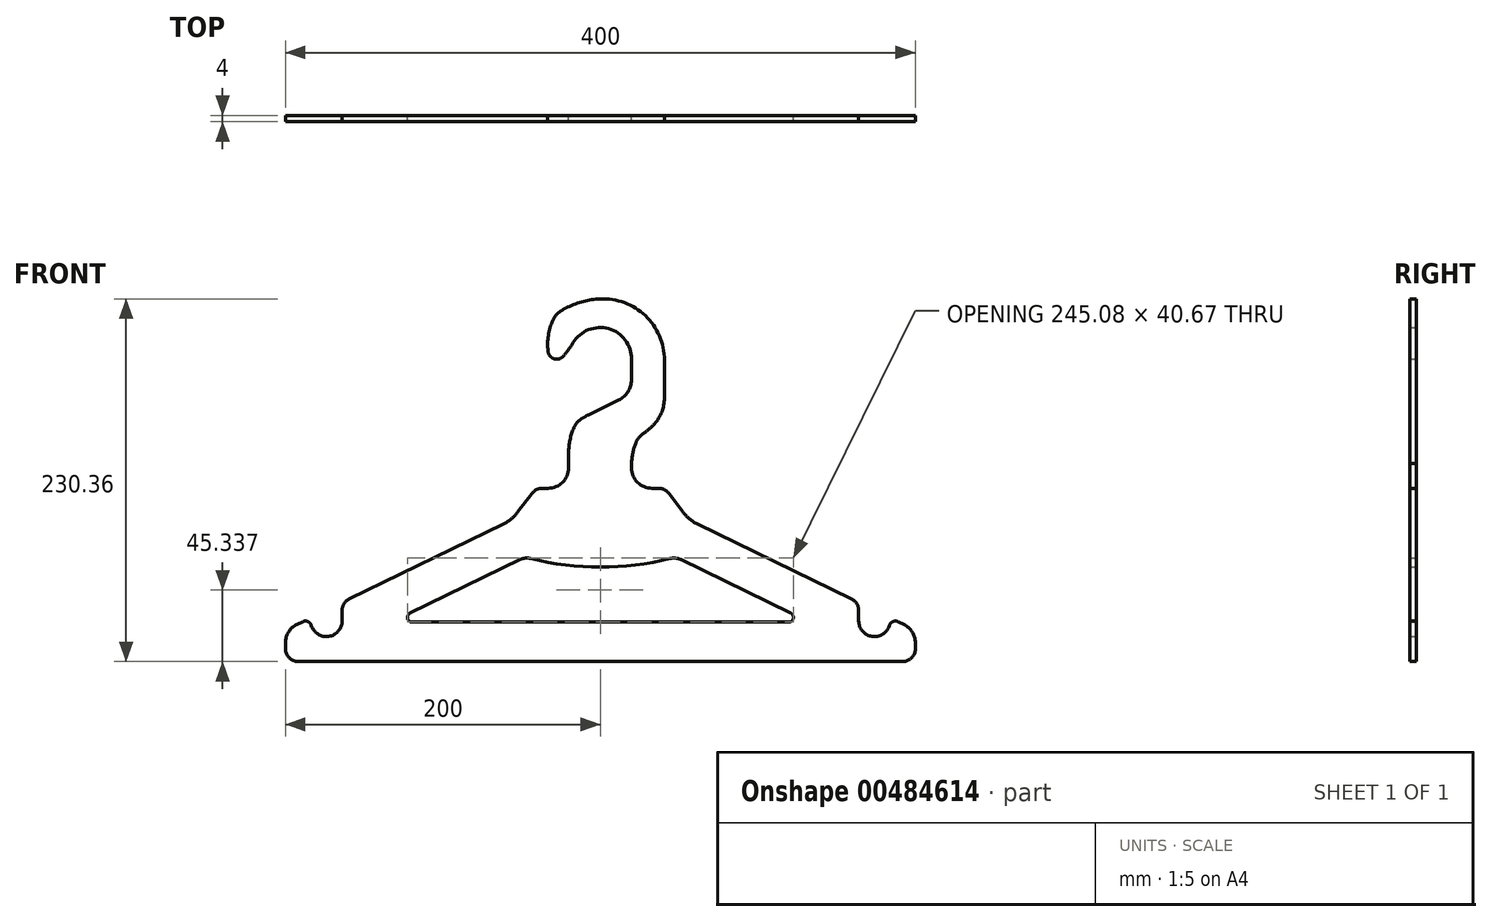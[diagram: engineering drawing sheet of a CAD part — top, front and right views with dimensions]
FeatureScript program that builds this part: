
annotation { "Feature Type Name" : "Feature", "Feature Type Description" : "" }
export const myFeature = defineFeature(function(context is Context, id is Id, definition is map)
    precondition{}
    {
        {
            var Q0;
            Q0=qCreatedBy(makeId("Front.planeOp"),FACE);
            var sketch = newSketch(context, id + "F0", { "sketchPlane" : qUnion([Q0])});
            skLineSegment(sketch, "E0", {"start": v(0, 0) * mm, "end": v(0, 266.9) * mm, "construction": true});
            skLineSegment(sketch, "E1", {"start": v(0, 0) * mm, "end": v(0, -107.96) * mm, "construction": true});
            skSolve(sketch);
        }
        {
            var Q0;
            Q0=qCreatedBy(makeId("Front.planeOp"),FACE);
            var sketch = newSketch(context, id + "F1", { "sketchPlane" : qUnion([Q0])});
            skLineSegment(sketch, "E2", {"start": v(0, 0) * mm, "end": v(-192, 0) * mm});
            skLineSegment(sketch, "E3", {"start": v(-200, 8) * mm, "end": v(-200, 11.87) * mm});
            skLineSegment(sketch, "E4", {"start": v(-192.69, 23.56) * mm, "end": v(-189.15, 25.28) * mm});
            skLineSegment(sketch, "E5", {"start": v(-52.5, 94.84) * mm, "end": v(-43.53, 106.8) * mm});
            skLineSegment(sketch, "E6", {"start": v(-37.13, 110) * mm, "end": v(0, 110) * mm});
            skPoint(sketch, "E7.visualSharp", {"position": v(-56.13, 90) * mm});
            skArc(sketch, "E7.filletArc", {"start": v(-61.56, 87.36) * mm, "mid": v(-56.58, 90.56) * mm, "end": v(-52.5, 94.84) * mm});
            skPoint(sketch, "E8.visualSharp", {"position": v(-41.13, 110) * mm});
            skArc(sketch, "E8.filletArc", {"start": v(-37.13, 110) * mm, "mid": v(-40.7, 109.16) * mm, "end": v(-43.53, 106.8) * mm});
            skPoint(sketch, "E9.visualSharp", {"position": v(-200, 20) * mm});
            skArc(sketch, "E9.filletArc", {"start": v(-192.69, 23.56) * mm, "mid": v(-198.02, 18.76) * mm, "end": v(-200, 11.87) * mm});
            skLineSegment(sketch, "E10.trimOffspring", {"start": v(-159.53, 39.69) * mm, "end": v(-61.56, 87.36) * mm});
            skPoint(sketch, "E11.visualSharp", {"position": v(-200, 0) * mm});
            skArc(sketch, "E11.filletArc", {"start": v(-200, 8) * mm, "mid": v(-197.66, 2.34) * mm, "end": v(-192, 0) * mm});
            skArc(sketch, "E12.MirrorCS", {"start": v(200, 8) * mm, "mid": v(197.66, 2.34) * mm, "end": v(192, 0) * mm});
            skArc(sketch, "E13.MirrorCS", {"start": v(37.13, 110) * mm, "mid": v(40.7, 109.16) * mm, "end": v(43.53, 106.8) * mm});
            skLineSegment(sketch, "E14.MirrorCS", {"start": v(200, 8) * mm, "end": v(200, 11.87) * mm});
            skArc(sketch, "E15.MirrorCS", {"start": v(192.69, 23.56) * mm, "mid": v(198.02, 18.76) * mm, "end": v(200, 11.87) * mm});
            skArc(sketch, "E16.MirrorCS", {"start": v(61.56, 87.36) * mm, "mid": v(56.58, 90.56) * mm, "end": v(52.5, 94.84) * mm});
            skPoint(sketch, "E17.MirrorP", {"position": v(56.13, 90) * mm});
            skLineSegment(sketch, "E18.MirrorCS", {"start": v(37.13, 110) * mm, "end": v(0, 110) * mm});
            skLineSegment(sketch, "E19.MirrorCS", {"start": v(52.5, 94.84) * mm, "end": v(43.53, 106.8) * mm});
            skPoint(sketch, "E20.MirrorP", {"position": v(41.13, 110) * mm});
            skPoint(sketch, "E21.MirrorP", {"position": v(200, 0) * mm});
            skPoint(sketch, "E22.MirrorP", {"position": v(200, 20) * mm});
            skLineSegment(sketch, "E23.MirrorCS", {"start": v(0, 0) * mm, "end": v(192, 0) * mm});
            skLineSegment(sketch, "E24", {"start": v(-164.03, 32.5) * mm, "end": v(-164.03, 25.82) * mm});
            skArc(sketch, "E25", {"start": v(-164.03, 25.82) * mm, "mid": v(-172.54, 15.93) * mm, "end": v(-183.58, 22.86) * mm});
            skPoint(sketch, "E26.visualSharp", {"position": v(-164.03, 37.5) * mm});
            skArc(sketch, "E26.filletArc", {"start": v(-159.53, 39.69) * mm, "mid": v(-162.81, 36.74) * mm, "end": v(-164.03, 32.5) * mm});
            skPoint(sketch, "E27.visualSharp", {"position": v(-183.82, 27.87) * mm});
            skArc(sketch, "E27.filletArc", {"start": v(-183.58, 22.86) * mm, "mid": v(-185.81, 25.35) * mm, "end": v(-189.15, 25.28) * mm});
            skLineSegment(sketch, "E28.MirrorCS", {"start": v(159.53, 39.69) * mm, "end": v(61.56, 87.36) * mm});
            skArc(sketch, "E29.MirrorCS", {"start": v(183.58, 22.86) * mm, "mid": v(185.81, 25.35) * mm, "end": v(189.15, 25.28) * mm});
            skArc(sketch, "E30.MirrorCS", {"start": v(164.03, 25.82) * mm, "mid": v(172.54, 15.93) * mm, "end": v(183.58, 22.86) * mm});
            skLineSegment(sketch, "E31.MirrorCS", {"start": v(164.03, 32.5) * mm, "end": v(164.03, 25.82) * mm});
            skArc(sketch, "E32.MirrorCS", {"start": v(159.53, 39.69) * mm, "mid": v(162.81, 36.74) * mm, "end": v(164.03, 32.5) * mm});
            skLineSegment(sketch, "E33.MirrorCS", {"start": v(192.69, 23.56) * mm, "end": v(189.15, 25.28) * mm});
            skSolve(sketch);
        }
        {
            var Q0;
            Q0=qCreatedBy(makeId("Front.planeOp"),FACE);
            var sketch = newSketch(context, id + "F2", { "sketchPlane" : qUnion([Q0])});
            skLineSegment(sketch, "E34.0", {"start": v(-120.87, 30.7) * mm, "end": v(-51.05, 64.67) * mm});
            skLineSegment(sketch, "E35.0", {"start": v(0, 25) * mm, "end": v(-119.56, 25) * mm});
            skLineSegment(sketch, "E36", {"start": v(-25.94, 60) * mm, "end": v(21.34, 60) * mm, "construction": true});
            skArc(sketch, "E37", {"start": v(-44.28, 65.38) * mm, "mid": v(-22.3, 61.35) * mm, "end": v(0, 60) * mm});
            skPoint(sketch, "E38.visualSharp", {"position": v(-47.74, 66.28) * mm});
            skArc(sketch, "E38.filletArc", {"start": v(-44.28, 65.38) * mm, "mid": v(-47.73, 65.62) * mm, "end": v(-51.05, 64.67) * mm});
            skPoint(sketch, "E39.visualSharp", {"position": v(-132.58, 25) * mm});
            skArc(sketch, "E39.filletArc", {"start": v(-120.87, 30.7) * mm, "mid": v(-122.48, 27.33) * mm, "end": v(-119.56, 25) * mm});
            skArc(sketch, "E40.MirrorCS", {"start": v(120.87, 30.7) * mm, "mid": v(122.48, 27.33) * mm, "end": v(119.56, 25) * mm});
            skArc(sketch, "E41.MirrorCS", {"start": v(44.28, 65.38) * mm, "mid": v(47.73, 65.62) * mm, "end": v(51.05, 64.67) * mm});
            skPoint(sketch, "E42.MirrorP", {"position": v(132.58, 25) * mm});
            skPoint(sketch, "E43.MirrorP", {"position": v(47.74, 66.28) * mm});
            skLineSegment(sketch, "E44.MirrorCS", {"start": v(120.87, 30.7) * mm, "end": v(51.05, 64.67) * mm});
            skArc(sketch, "E45.MirrorCS", {"start": v(44.28, 65.38) * mm, "mid": v(22.3, 61.35) * mm, "end": v(0, 60) * mm});
            skLineSegment(sketch, "E46.MirrorCS", {"start": v(0, 25) * mm, "end": v(119.56, 25) * mm});
            skSolve(sketch);
        }
        {
            var Q0;
            Q0=qCreatedBy(makeId("Front.planeOp"),FACE);
            var sketch = newSketch(context, id + "F3", { "sketchPlane" : qUnion([Q0])});
            skPoint(sketch, "E47.0", {"position": v(-0.2, 110) * mm});
            skLineSegment(sketch, "E48.0", {"start": v(-35.32, 110) * mm, "end": v(-33.2, 110) * mm});
            skLineSegment(sketch, "E48.1", {"start": v(34.93, 110) * mm, "end": v(32.8, 110) * mm});
            skLineSegment(sketch, "E49", {"start": v(19.8, 123) * mm, "end": v(19.8, 125.83) * mm});
            skCircle(sketch, "E50", {"center": v(-0.2, 192.06) * mm, "radius": 20 * mm, "construction": true});
            skLineSegment(sketch, "E51", {"start": v(-7.5, 156.72) * mm, "end": v(11.55, 165.98) * mm});
            skArc(sketch, "E52", {"start": v(-7.5, 156.72) * mm, "mid": v(-9.89, 155.45) * mm, "end": v(-12.2, 154.03) * mm});
            skArc(sketch, "E53", {"start": v(-12.2, 154.03) * mm, "mid": v(-14.85, 151.67) * mm, "end": v(-16.74, 148.67) * mm});
            skArc(sketch, "E54", {"start": v(-16.74, 148.67) * mm, "mid": v(-19.32, 140.79) * mm, "end": v(-20.2, 132.54) * mm});
            skLineSegment(sketch, "E55", {"start": v(-20.2, 123) * mm, "end": v(-20.2, 132.54) * mm});
            skArc(sketch, "E56", {"start": v(34.37, 150.98) * mm, "mid": v(31.01, 147.7) * mm, "end": v(27.27, 144.85) * mm});
            skArc(sketch, "E57", {"start": v(27.27, 144.85) * mm, "mid": v(24.42, 142.25) * mm, "end": v(22.48, 138.91) * mm});
            skArc(sketch, "E58", {"start": v(22.48, 138.91) * mm, "mid": v(20.36, 131.27) * mm, "end": v(19.8, 123.36) * mm});
            skArc(sketch, "E59", {"start": v(11.55, 165.98) * mm, "mid": v(17.44, 171.24) * mm, "end": v(19.69, 178.8) * mm});
            skLineSegment(sketch, "E60", {"start": v(19.69, 178.8) * mm, "end": v(19.86, 192.06) * mm});
            skArc(sketch, "E61", {"start": v(19.86, 192.06) * mm, "mid": v(5.23, 211.36) * mm, "end": v(-17.3, 202.5) * mm});
            skArc(sketch, "E62", {"start": v(-33.3, 197.08) * mm, "mid": v(-29.37, 192.28) * mm, "end": v(-23.42, 194.03) * mm});
            skArc(sketch, "E63", {"start": v(-23.42, 194.03) * mm, "mid": v(-20.2, 198.15) * mm, "end": v(-17.3, 202.5) * mm});
            skArc(sketch, "E64", {"start": v(-20.88, 225) * mm, "mid": v(-23.28, 223.73) * mm, "end": v(-25.59, 222.31) * mm});
            skArc(sketch, "E65", {"start": v(-25.59, 222.31) * mm, "mid": v(-28.27, 219.91) * mm, "end": v(-30.18, 216.85) * mm});
            skArc(sketch, "E66", {"start": v(-30.18, 216.85) * mm, "mid": v(-33.01, 207.17) * mm, "end": v(-33.3, 197.08) * mm});
            skArc(sketch, "E67", {"start": v(-20.88, 225) * mm, "mid": v(-10.8, 228.7) * mm, "end": v(-0.2, 230.32) * mm});
            skArc(sketch, "E68", {"start": v(-0.2, 230.32) * mm, "mid": v(28.56, 219.65) * mm, "end": v(40.65, 191.46) * mm});
            skLineSegment(sketch, "E69", {"start": v(40.65, 167.33) * mm, "end": v(40.65, 191.46) * mm});
            skArc(sketch, "E70.filletArc", {"start": v(-33.2, 110) * mm, "mid": v(-24, 113.8) * mm, "end": v(-20.2, 123) * mm});
            skArc(sketch, "E71.filletArc", {"start": v(19.8, 123) * mm, "mid": v(23.62, 113.8) * mm, "end": v(32.8, 110) * mm});
            skArc(sketch, "E72", {"start": v(34.37, 150.98) * mm, "mid": v(39.02, 158.57) * mm, "end": v(40.65, 167.33) * mm});
            skLineSegment(sketch, "E73", {"start": v(-33.2, 110) * mm, "end": v(32.8, 110) * mm});
            skSolve(sketch);
        }
        {
            var Q0;
            Q0 = qSketchRegion(id + "F1", true);
            extrude(context, id + "F4", {"entities" : qUnion([Q0]), "depth" : 4 * mm, "offsetDistance" : 25 * mm});
        }
        {
            var Q0;
            Q0 = qSketchRegion(id + "F2", true);
            extrude(context, id + "F5", {"entities" : qUnion([Q0]), "operationType" : NewBodyOperationType.REMOVE, "depth" : 25 * mm, "offsetDistance" : 25 * mm});
        }
        {
            var Q0;
            Q0 = qSketchRegion(id + "F3", true);
            extrude(context, id + "F6", {"entities" : qUnion([Q0]), "operationType" : NewBodyOperationType.ADD, "depth" : 4 * mm, "offsetDistance" : 25 * mm});
        }
    });
